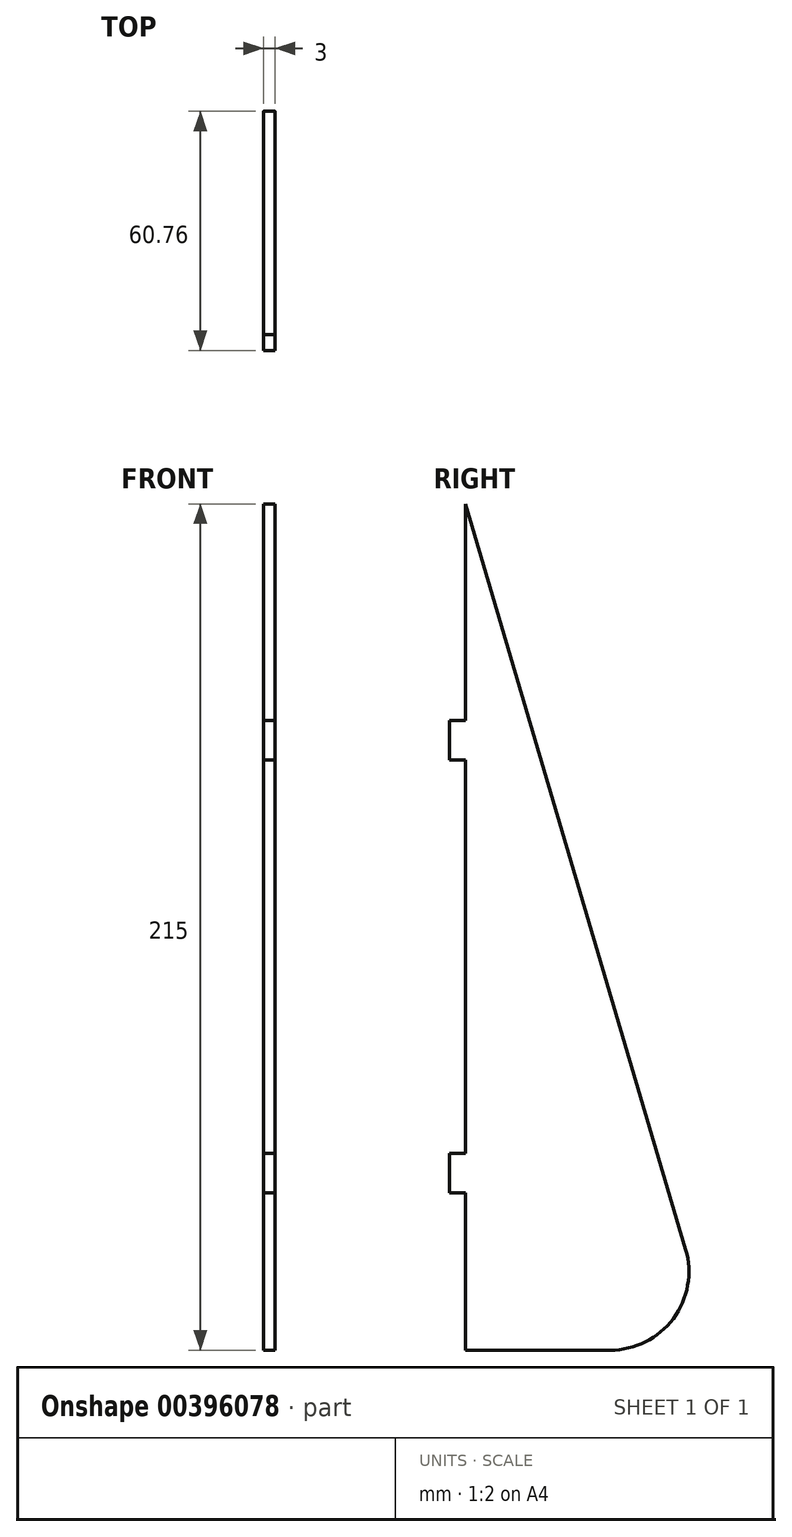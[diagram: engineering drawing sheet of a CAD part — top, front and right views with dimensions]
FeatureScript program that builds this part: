
annotation { "Feature Type Name" : "Feature", "Feature Type Description" : "" }
export const myFeature = defineFeature(function(context is Context, id is Id, definition is map)
    precondition{}
    {
        {
            var Q0;
            Q0=qCreatedBy(makeId("Right.planeOp"),FACE);
            var sketch = newSketch(context, id + "F0", { "sketchPlane" : qUnion([Q0])});
            skLineSegment(sketch, "E0", {"start": v(0, 220) * mm, "end": v(55.94, 30.67) * mm});
            skLineSegment(sketch, "E1", {"start": v(0, 5) * mm, "end": v(0, 220) * mm});
            skLineSegment(sketch, "E2", {"start": v(0, 165) * mm, "end": v(-4, 165) * mm});
            skLineSegment(sketch, "E3", {"start": v(-4, 165) * mm, "end": v(-4, 155) * mm});
            skLineSegment(sketch, "E4", {"start": v(-4, 155) * mm, "end": v(0, 155) * mm});
            skLineSegment(sketch, "E5", {"start": v(0, 55) * mm, "end": v(-4, 55) * mm});
            skLineSegment(sketch, "E6", {"start": v(-4, 55) * mm, "end": v(-4, 45) * mm});
            skLineSegment(sketch, "E7", {"start": v(-4, 45) * mm, "end": v(0, 45) * mm});
            skPoint(sketch, "E8.visualSharp", {"position": v(65, 0) * mm});
            skPoint(sketch, "E9.end.orphan", {"position": v(0, 0) * mm});
            skLineSegment(sketch, "E10", {"start": v(0, 5) * mm, "end": v(36.76, 5) * mm});
            skPoint(sketch, "E11.visualSharp", {"position": v(63.52, 5) * mm});
            skArc(sketch, "E11.filletArc", {"start": v(36.76, 5) * mm, "mid": v(52.78, 13.03) * mm, "end": v(55.94, 30.67) * mm});
            skSolve(sketch);
        }
        {
            var Q0;
            Q0=qSketchRegion(id+"F0",true);
            extrude(context, id + "F1", {"entities" : qUnion([Q0]), "depth" : 3 * mm});
        }
    });
